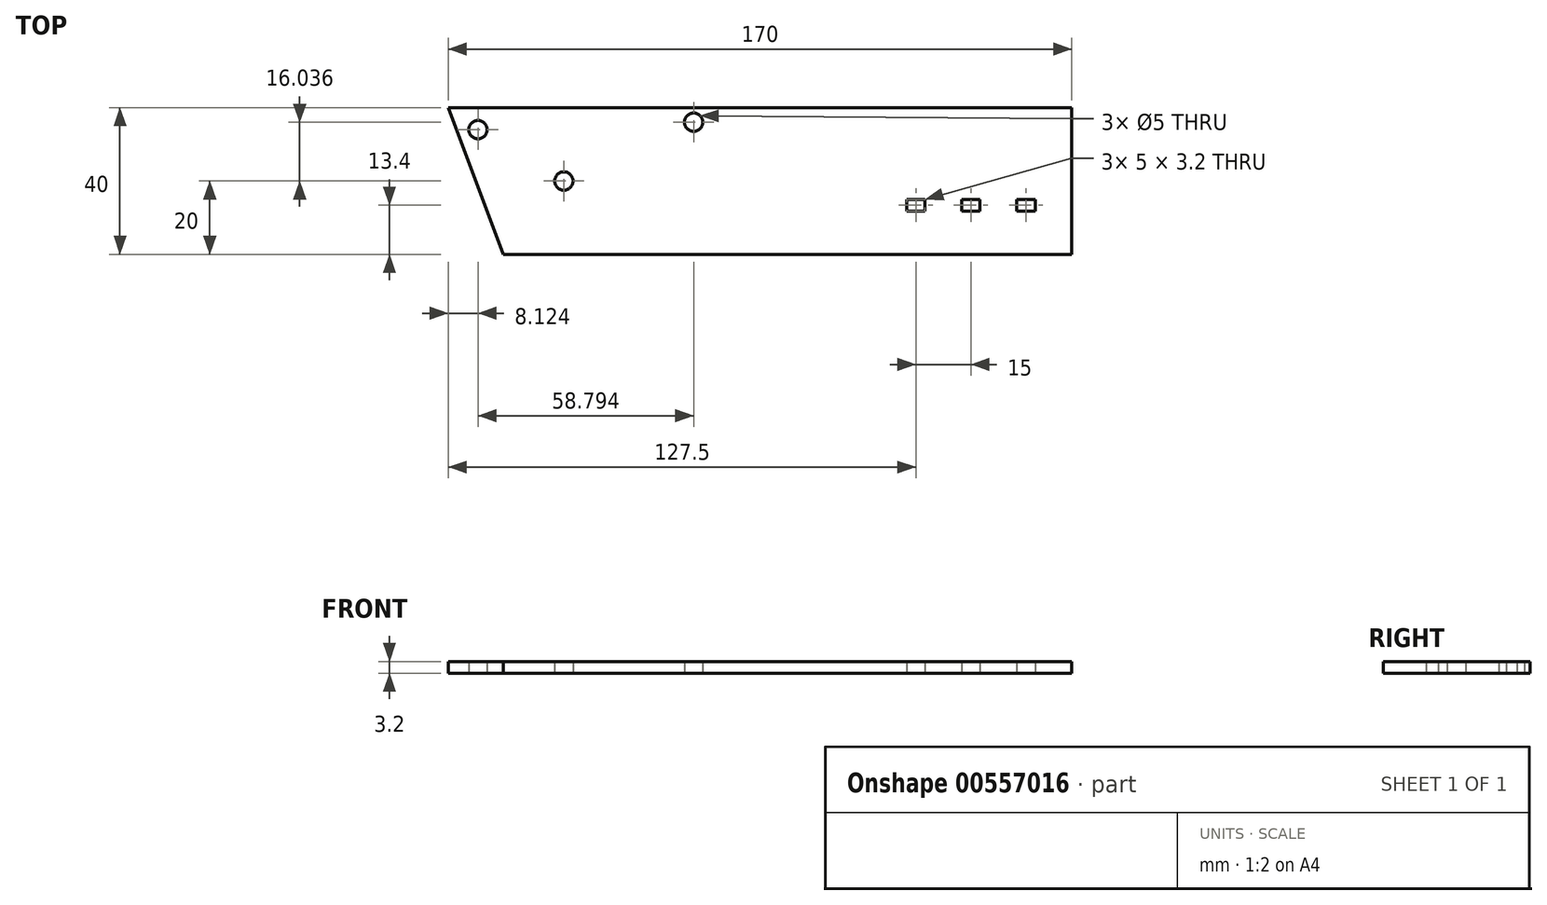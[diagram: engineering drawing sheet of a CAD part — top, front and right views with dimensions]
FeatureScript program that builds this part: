
annotation { "Feature Type Name" : "Feature", "Feature Type Description" : "" }
export const myFeature = defineFeature(function(context is Context, id is Id, definition is map)
    precondition{}
    {
        {
            var Q0;
            Q0=qCreatedBy(makeId("Top.planeOp"),FACE);
            var sketch = newSketch(context, id + "F0", { "sketchPlane" : qUnion([Q0])});
            skLineSegment(sketch, "E0.bottom", {"start": v(85, -20) * mm, "end": v(-70, -20) * mm});
            skLineSegment(sketch, "E0.top", {"start": v(85, 20) * mm, "end": v(-85, 20) * mm});
            skLineSegment(sketch, "E0.left", {"start": v(85, -20) * mm, "end": v(85, 20) * mm});
            skPoint(sketch, "E0.middle", {"position": v(0, 0) * mm});
            skLineSegment(sketch, "E1", {"start": v(-85, 20) * mm, "end": v(-70, -20) * mm});
            skLineSegment(sketch, "E2.bottom", {"start": v(70, -5) * mm, "end": v(75, -5) * mm});
            skLineSegment(sketch, "E2.top", {"start": v(70, -8.2) * mm, "end": v(75, -8.2) * mm});
            skLineSegment(sketch, "E2.left", {"start": v(70, -5) * mm, "end": v(70, -8.2) * mm});
            skLineSegment(sketch, "E2.right", {"start": v(75, -5) * mm, "end": v(75, -8.2) * mm});
            skLineSegment(sketch, "E3.bottom", {"start": v(55, -5) * mm, "end": v(60, -5) * mm});
            skLineSegment(sketch, "E3.top", {"start": v(55, -8.2) * mm, "end": v(60, -8.2) * mm});
            skLineSegment(sketch, "E3.left", {"start": v(55, -5) * mm, "end": v(55, -8.2) * mm});
            skLineSegment(sketch, "E3.right", {"start": v(60, -5) * mm, "end": v(60, -8.2) * mm});
            skLineSegment(sketch, "E4.bottom", {"start": v(40, -5) * mm, "end": v(45, -5) * mm});
            skLineSegment(sketch, "E4.top", {"start": v(40, -8.2) * mm, "end": v(45, -8.2) * mm});
            skLineSegment(sketch, "E4.left", {"start": v(40, -5) * mm, "end": v(40, -8.2) * mm});
            skLineSegment(sketch, "E4.right", {"start": v(45, -5) * mm, "end": v(45, -8.2) * mm});
            skPoint(sketch, "E0.right.start.orphan", {"position": v(-85, -20) * mm});
            skCircle(sketch, "E5", {"center": v(-53.47, 0) * mm, "radius": 2.5 * mm});
            skCircle(sketch, "E6", {"center": v(-76.88, 14) * mm, "radius": 2.5 * mm});
            skCircle(sketch, "E7", {"center": v(-18.08, 16.04) * mm, "radius": 2.5 * mm});
            skSolve(sketch);
        }
        {
            var Q0;
            Q0=qSketchRegion(id+"F0",true);
            extrude(context, id + "F1", {"entities" : qUnion([Q0]), "depth" : 3.2 * mm});
        }
    });
